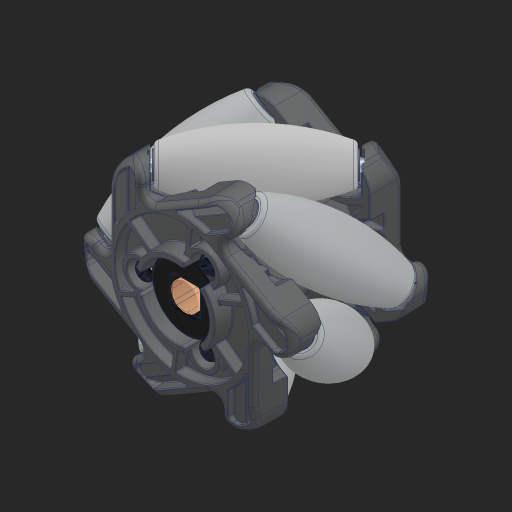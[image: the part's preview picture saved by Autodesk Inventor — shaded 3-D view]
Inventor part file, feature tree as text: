
AUTODESK INVENTOR PART (.ipt)
format: ipt  version: 2023 (Build 270158000, 158)  size: 56,157,696 bytes
history: native  units: in
note: dims shown in document units (in); Inventor stores cm internally (conversion verified against a paired STEP export)
features: other x38, sketch x1
ambient origin geometry x8: Origin, YZ Plane, XZ Plane, XY Plane, X Axis, Y Axis, Z Axis, Center Point
bodies: Solid3 (feature_tree), Solid4 (feature_tree), Solid5 (feature_tree), Solid8 (feature_tree), Solid9 (feature_tree), Solid10 (feature_tree), Solid13 (feature_tree), Solid14 (feature_tree), Solid15 (feature_tree), Solid18 (feature_tree), Solid19 (feature_tree), Solid20 (feature_tree), Solid23 (feature_tree), Solid24 (feature_tree), Solid25 (feature_tree), Solid28 (feature_tree), Solid29 (feature_tree), Solid30 (feature_tree), Solid31 (feature_tree), Solid32 (feature_tree), Solid33 (feature_tree), Solid34 (feature_tree), Solid35 (feature_tree), Solid36 (feature_tree), Solid37 (feature_tree), Solid38 (feature_tree), Solid39 (feature_tree), Solid40 (feature_tree)
feature tree (39):
  other  "2 Mecanum Right.ipt"
  other  "Solid2::2 Mecanum Right.ipt"
  other  "Solid3::2 Mecanum Right.ipt"
  other  "Solid4::2 Mecanum Right.ipt"
  other  "Solid5::2 Mecanum Right.ipt"
  other  "Solid7::2 Mecanum Right.ipt"
  other  "Solid8::2 Mecanum Right.ipt"
  other  "Solid9::2 Mecanum Right.ipt"
  other  "Solid10::2 Mecanum Right.ipt"
  other  "Solid12::2 Mecanum Right.ipt"
  other  "Solid13::2 Mecanum Right.ipt"
  other  "Solid14::2 Mecanum Right.ipt"
  other  "Solid15::2 Mecanum Right.ipt"
  other  "Solid17::2 Mecanum Right.ipt"
  other  "Solid18::2 Mecanum Right.ipt"
  other  "Solid19::2 Mecanum Right.ipt"
  other  "Solid20::2 Mecanum Right.ipt"
  other  "Solid22::2 Mecanum Right.ipt"
  other  "Solid23::2 Mecanum Right.ipt"
  other  "Solid24::2 Mecanum Right.ipt"
  other  "Solid25::2 Mecanum Right.ipt"
  other  "Solid27::2 Mecanum Right.ipt"
  other  "Solid28::2 Mecanum Right.ipt"
  other  "Solid29::2 Mecanum Right.ipt"
  other  "Solid30::2 Mecanum Right.ipt"
  other  "Solid31::2 Mecanum Right.ipt"
  other  "Solid32::2 Mecanum Right.ipt"
  other  "Solid33::2 Mecanum Right.ipt"
  other  "Solid34::2 Mecanum Right.ipt"
  other  "Solid35::2 Mecanum Right.ipt"
  other  "Solid36::2 Mecanum Right.ipt"
  other  "Solid37::2 Mecanum Right.ipt"
  other  "Solid38::2 Mecanum Right.ipt"
  other  "Solid39::2 Mecanum Right.ipt"
  other  "Solid40::2 Mecanum Right.ipt"
  other  "TaggingFeature1"
  sketch  "Sketch1"  dims[d0=0.3937in]
  other  "Srf1"
  other  "Srf1::Derived"
